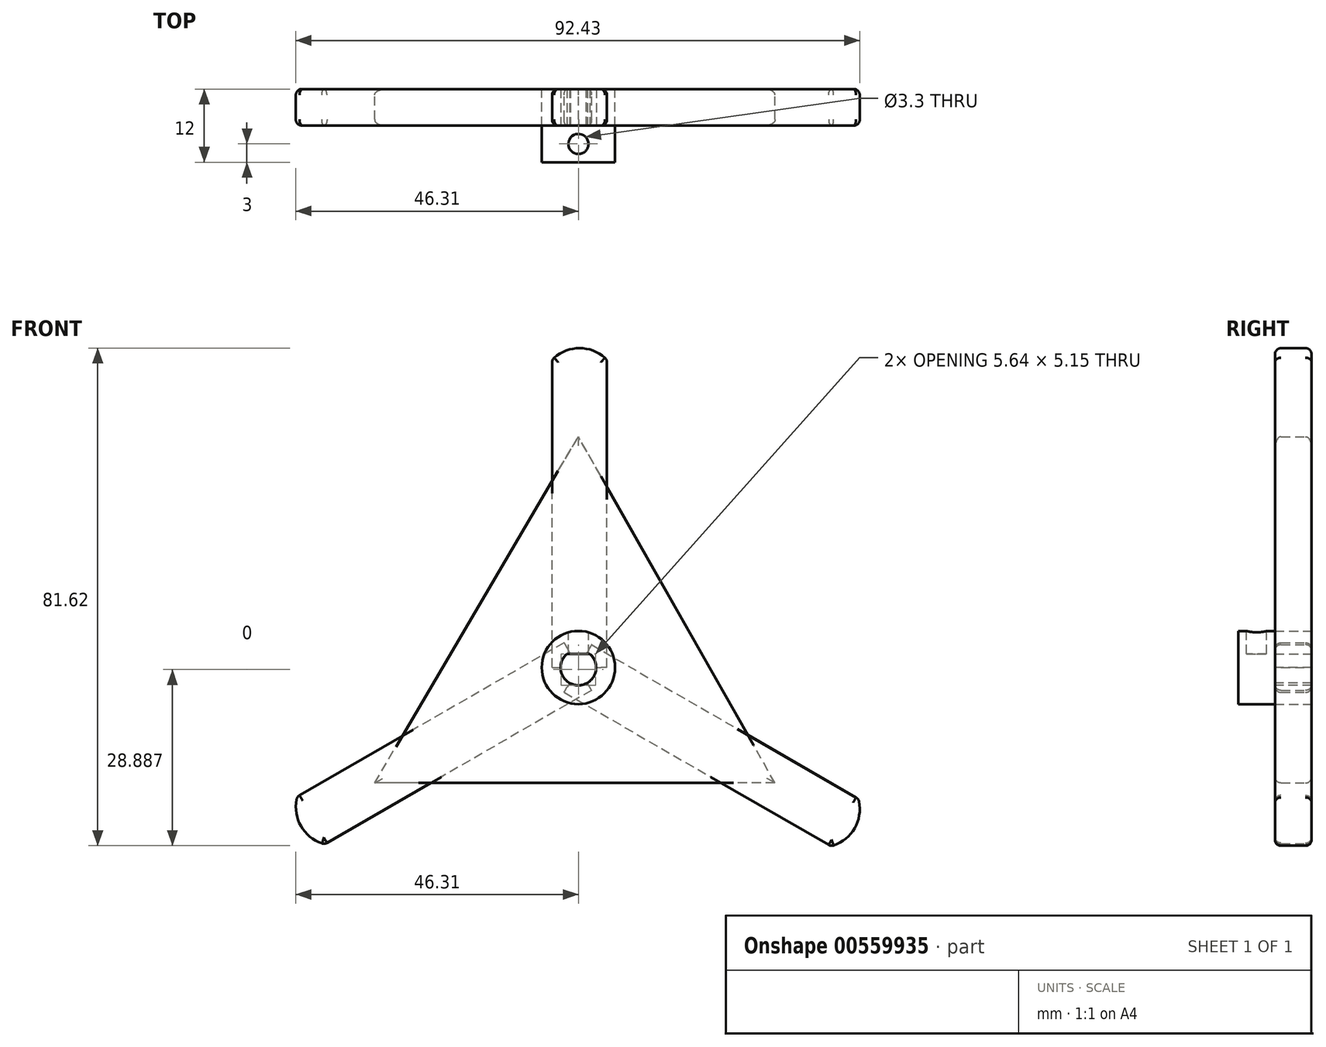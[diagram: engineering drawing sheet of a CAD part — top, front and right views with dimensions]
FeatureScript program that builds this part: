
annotation { "Feature Type Name" : "Feature", "Feature Type Description" : "" }
export const myFeature = defineFeature(function(context is Context, id is Id, definition is map)
    precondition{}
    {
        {
            assignVariable(context, id + "F0", {"name" : "thick", "anyValue" : 6});
        }
        {
            assignVariable(context, id + "F1", {"name" : "bushingWide", "anyValue" : 12});
        }
        {
            assignVariable(context, id + "F2", {"name" : "bushingDiam", "anyValue" : 12});
        }
        {
            assignVariable(context, id + "F3", {"name" : "filletRad", "anyValue" : 1});
        }
        {
            var Q0;
            Q0=qCreatedBy(makeId("Front.planeOp"),FACE);
            var sketch = newSketch(context, id + "F4", { "sketchPlane" : qUnion([Q0])});
            skLineSegment(sketch, "E0.bottom", {"start": v(-4.3, 0) * mm, "end": v(4.7, 0) * mm});
            skLineSegment(sketch, "E0.top", {"start": v(-4.3, 50.5) * mm, "end": v(4.7, 50.5) * mm});
            skLineSegment(sketch, "E0.left", {"start": v(-4.3, 0) * mm, "end": v(-4.3, 50.5) * mm});
            skLineSegment(sketch, "E0.right", {"start": v(4.7, 0) * mm, "end": v(4.7, 50.5) * mm});
            skArc(sketch, "E1", {"start": v(4.7, 50.5) * mm, "mid": v(0.2, 52.4) * mm, "end": v(-4.3, 50.5) * mm});
            skSolve(sketch);
        }
        {
            var Q0;
            Q0=qCreatedBy(makeId("Right.planeOp"),FACE);
            var sketch = newSketch(context, id + "F5", { "sketchPlane" : qUnion([Q0])});
            skLineSegment(sketch, "E2", {"start": v(0, 0) * mm, "end": v(-42.63, 0) * mm});
            skSolve(sketch);
        }
        {
            var Q0;
            Q0 = qSketchRegion(id + "F4", true);
            extrude(context, id + "F6", {"entities" : qUnion([Q0]), "depth" : (getVariable(context, 'thick')) * mm, "offsetDistance" : 25 * mm});
        }
        {
            var Q0;
            Q0=makeQuery(id+"F6.opExtrude","SWEPT_BODY",BODY,{"disambiguationData":[OSD([sQuery(id+"F4.wireOp",EDGE,"E0.bottom"),sQuery(id+"F4.wireOp",EDGE,"E0.left"),sQuery(id+"F4.wireOp",EDGE,"E0.right"),sQuery(id+"F4.wireOp",EDGE,"E1")])]});
            var Q1;
            Q1=sQuery(id+"F5.wireOp",EDGE,"E2");
            transform(context, id + "F7", {"entities" : qUnion([Q0]), "transformType" : TransformType.ROTATION, "transformAxis" : qUnion([Q1]), "angle" : 120 * degree, "makeCopy" : true});
        }
        {
            var Q0;
            Q0=makeQuery(id+"F6.opExtrude","SWEPT_BODY",BODY,{"disambiguationData":[OSD([sQuery(id+"F4.wireOp",EDGE,"E0.bottom"),sQuery(id+"F4.wireOp",EDGE,"E0.left"),sQuery(id+"F4.wireOp",EDGE,"E0.right"),sQuery(id+"F4.wireOp",EDGE,"E1")])]});
            var Q1;
            Q1=sQuery(id+"F5.wireOp",EDGE,"E2");
            transform(context, id + "F8", {"entities" : qUnion([Q0]), "transformType" : TransformType.ROTATION, "transformAxis" : qUnion([Q1]), "angle" : 240 * degree, "makeCopy" : true});
        }
        {
            var Q0;
            Q0=qCreatedBy(makeId("Front.planeOp"),FACE);
            var sketch = newSketch(context, id + "F9", { "sketchPlane" : qUnion([Q0])});
            skLineSegment(sketch, "E3", {"start": v(-1.88, 2.23) * mm, "end": v(1.88, 2.23) * mm});
            skCircle(sketch, "E4", {"center": v(0, 0) * mm, "radius": 6 * mm});
            skArc(sketch, "E5", {"start": v(-1.88, 2.23) * mm, "mid": v(0, -2.92) * mm, "end": v(1.88, 2.23) * mm});
            skSolve(sketch);
        }
        {
            var Q0;
            Q0=qCreatedBy(makeId("Front.planeOp"),FACE);
            var sketch = newSketch(context, id + "F10", { "sketchPlane" : qUnion([Q0])});
            skLineSegment(sketch, "E6", {"start": v(0, 0) * mm, "end": v(32.23, -18.94) * mm});
            skLineSegment(sketch, "E7", {"start": v(0, 0) * mm, "end": v(-33.39, -18.94) * mm});
            skLineSegment(sketch, "E8", {"start": v(0, 0) * mm, "end": v(0, 37.88) * mm});
            skLineSegment(sketch, "E9", {"start": v(-33.39, -18.94) * mm, "end": v(0, 37.88) * mm});
            skLineSegment(sketch, "E10", {"start": v(32.23, -18.94) * mm, "end": v(0, 37.88) * mm});
            skLineSegment(sketch, "E11", {"start": v(32.23, -18.94) * mm, "end": v(-33.39, -18.94) * mm});
            skSolve(sketch);
        }
        {
            var Q0;
            Q0=makeQuery(id+"F10.imprint","IMPRINT",FACE,{"disambiguationData":[TD([[makeQuery(id+"F10.imprint","IMPRINT",EDGE,{"derivedFrom":sQuery(id+"F10.wireOp",EDGE,"E7")}),-1.0]])]});
            var Q1;
            Q1=makeQuery(id+"F10.imprint","IMPRINT",FACE,{"disambiguationData":[TD([[makeQuery(id+"F10.imprint","IMPRINT",EDGE,{"derivedFrom":sQuery(id+"F10.wireOp",EDGE,"E6")}),1.0]])]});
            var Q2;
            Q2=makeQuery(id+"F10.imprint","IMPRINT",FACE,{"disambiguationData":[TD([[makeQuery(id+"F10.imprint","IMPRINT",EDGE,{"derivedFrom":sQuery(id+"F10.wireOp",EDGE,"E6")}),-1.0]])]});
            extrude(context, id + "F11", {"entities" : qUnion([Q0, Q1, Q2]), "depth" : (getVariable(context, 'thick')) * mm, "offsetDistance" : 25 * mm});
        }
        {
            var Q0;
            Q0 = qSketchRegion(id + "F9", true);
            extrude(context, id + "F12", {"entities" : qUnion([Q0]), "depth" : (getVariable(context, 'bushingWide')) * mm, "offsetDistance" : 25 * mm});
        }
        {
            var Q0;
            Q0=qCreatedBy(makeId("Top.planeOp"),FACE);
            cPlane(context, id + "F13", {"entities" : qUnion([Q0]), "cplaneType" : CPlaneType.OFFSET, "offset" : (getVariable(context, 'bushingDiam') / 2) * mm, "width" : 150 * mm, "height" : 150 * mm});
        }
        {
            var Q0;
            Q0=qCreatedBy(id+"F13.planeOp",FACE);
            var sketch = newSketch(context, id + "F14", { "sketchPlane" : qUnion([Q0])});
            skPoint(sketch, "E12", {"position": v(0, -9) * mm});
            skSolve(sketch);
        }
        {
            var Q0;
            Q0=sQuery(id+"F14.wireOp",VERTEX,"E12");
            var Q1;
            Q1=makeQuery(id+"F12.opExtrude","SWEPT_BODY",BODY,{"disambiguationData":[OSD([sQuery(id+"F9.wireOp",EDGE,"E3"),sQuery(id+"F9.wireOp",EDGE,"E4"),sQuery(id+"F9.wireOp",EDGE,"E5")])]});
            hole(context, id + "F15", {"style" : HoleStyle.SIMPLE, "endStyle" : HoleEndStyle.BLIND, "standardTappedOrClearance" : lookupTablePath({ "standard" : "ISO", "engagement" : "75%", "pitch" : "0.7 mm", "size" : "M4", "type" : "Tapped" }), "standardBlindInLast" : lookupTablePath({ "standard" : "ISO", "engagement" : "75%", "pitch" : "0.7 mm", "size" : "M4", "type" : "Tapped" }), "holeDiameter" : 3.3 * mm, "showTappedDepth" : true, "holeDepth" : 6 * mm, "isTappedThrough" : true, "tappedDepth" : (getVariable(context, 'bushingDiam') / 2) * mm, "tapClearance" : 0, "locations" : qUnion([Q0]), "scope" : qUnion([Q1]), "majorDiameter" : 4 * mm});
        }
        {
            var Q0;
            Q0=makeQuery(id+"F11.opExtrude","CAP_EDGE",EDGE,{"disambiguationData":[OSD([sQuery(id+"F10.wireOp",EDGE,"E9")])],"isStart":false});
            var Q1;
            Q1=makeQuery(id+"F6.opExtrude","CAP_EDGE",EDGE,{"disambiguationData":[OSD([sQuery(id+"F4.wireOp",EDGE,"E0.left")])],"isStart":false});
            var Q2;
            Q2=makeQuery(id+"F6.opExtrude","CAP_EDGE",EDGE,{"disambiguationData":[OSD([sQuery(id+"F4.wireOp",EDGE,"E1")])],"isStart":false});
            var Q3;
            Q3=makeQuery(id+"F6.opExtrude","CAP_EDGE",EDGE,{"disambiguationData":[OSD([sQuery(id+"F4.wireOp",EDGE,"E0.right")])],"isStart":false});
            var Q4;
            Q4=makeQuery(id+"F11.opExtrude","CAP_EDGE",EDGE,{"disambiguationData":[OSD([sQuery(id+"F10.wireOp",EDGE,"E10")])],"isStart":false});
            var Q5;
            Q5=makeQuery(id+"F8.opPattern","COPY",EDGE,{"derivedFrom":makeQuery(id+"F6.opExtrude","CAP_EDGE",EDGE,{"disambiguationData":[OSD([sQuery(id+"F4.wireOp",EDGE,"E0.left")])],"isStart":false}),"instanceName":"1"});
            var Q6;
            Q6=makeQuery(id+"F8.opPattern","COPY",EDGE,{"derivedFrom":makeQuery(id+"F6.opExtrude","CAP_EDGE",EDGE,{"disambiguationData":[OSD([sQuery(id+"F4.wireOp",EDGE,"E1")])],"isStart":false}),"instanceName":"1"});
            var Q7;
            Q7=makeQuery(id+"F11.opExtrude","CAP_EDGE",EDGE,{"disambiguationData":[OSD([sQuery(id+"F10.wireOp",EDGE,"E11")])],"isStart":false});
            var Q8;
            Q8=makeQuery(id+"F7.opPattern","COPY",EDGE,{"derivedFrom":makeQuery(id+"F6.opExtrude","CAP_EDGE",EDGE,{"disambiguationData":[OSD([sQuery(id+"F4.wireOp",EDGE,"E0.left")])],"isStart":false}),"instanceName":"1"});
            var Q9;
            Q9=makeQuery(id+"F8.opPattern","COPY",EDGE,{"derivedFrom":makeQuery(id+"F6.opExtrude","CAP_EDGE",EDGE,{"disambiguationData":[OSD([sQuery(id+"F4.wireOp",EDGE,"E0.right")])],"isStart":false}),"instanceName":"1"});
            var Q10;
            Q10=makeQuery(id+"F7.opPattern","COPY",EDGE,{"derivedFrom":makeQuery(id+"F6.opExtrude","CAP_EDGE",EDGE,{"disambiguationData":[OSD([sQuery(id+"F4.wireOp",EDGE,"E1")])],"isStart":false}),"instanceName":"1"});
            var Q11;
            Q11=makeQuery(id+"F7.opPattern","COPY",EDGE,{"derivedFrom":makeQuery(id+"F6.opExtrude","CAP_EDGE",EDGE,{"disambiguationData":[OSD([sQuery(id+"F4.wireOp",EDGE,"E0.right")])],"isStart":false}),"instanceName":"1"});
            fillet(context, id + "F16", {"entities" : qUnion([Q0, Q1, Q2, Q3, Q4, Q5, Q6, Q7, Q8, Q9, Q10, Q11]), "radius" : (getVariable(context, 'filletRad')) * mm, "tangentPropagation" : true, "allowEdgeOverflow" : false});
        }
        {
            var Q0;
            Q0=makeQuery(id+"F11.opExtrude","CAP_EDGE",EDGE,{"disambiguationData":[OSD([sQuery(id+"F10.wireOp",EDGE,"E11")])],"isStart":true});
            var Q1;
            Q1=makeQuery(id+"F7.opPattern","COPY",EDGE,{"derivedFrom":makeQuery(id+"F6.opExtrude","CAP_EDGE",EDGE,{"disambiguationData":[OSD([sQuery(id+"F4.wireOp",EDGE,"E0.left")])],"isStart":true}),"instanceName":"1"});
            var Q2;
            Q2=makeQuery(id+"F7.opPattern","COPY",EDGE,{"derivedFrom":makeQuery(id+"F6.opExtrude","CAP_EDGE",EDGE,{"disambiguationData":[OSD([sQuery(id+"F4.wireOp",EDGE,"E1")])],"isStart":true}),"instanceName":"1"});
            var Q3;
            Q3=makeQuery(id+"F7.opPattern","COPY",EDGE,{"derivedFrom":makeQuery(id+"F6.opExtrude","CAP_EDGE",EDGE,{"disambiguationData":[OSD([sQuery(id+"F4.wireOp",EDGE,"E0.right")])],"isStart":true}),"instanceName":"1"});
            var Q4;
            Q4=makeQuery(id+"F11.opExtrude","CAP_EDGE",EDGE,{"disambiguationData":[OSD([sQuery(id+"F10.wireOp",EDGE,"E9")])],"isStart":true});
            var Q5;
            Q5=makeQuery(id+"F6.opExtrude","CAP_EDGE",EDGE,{"disambiguationData":[OSD([sQuery(id+"F4.wireOp",EDGE,"E1")])],"isStart":true});
            var Q6;
            Q6=makeQuery(id+"F6.opExtrude","CAP_EDGE",EDGE,{"disambiguationData":[OSD([sQuery(id+"F4.wireOp",EDGE,"E0.left")])],"isStart":true});
            var Q7;
            Q7=makeQuery(id+"F11.opExtrude","CAP_EDGE",EDGE,{"disambiguationData":[OSD([sQuery(id+"F10.wireOp",EDGE,"E10")])],"isStart":true});
            var Q8;
            Q8=makeQuery(id+"F8.opPattern","COPY",EDGE,{"derivedFrom":makeQuery(id+"F6.opExtrude","CAP_EDGE",EDGE,{"disambiguationData":[OSD([sQuery(id+"F4.wireOp",EDGE,"E0.left")])],"isStart":true}),"instanceName":"1"});
            var Q9;
            Q9=makeQuery(id+"F8.opPattern","COPY",EDGE,{"derivedFrom":makeQuery(id+"F6.opExtrude","CAP_EDGE",EDGE,{"disambiguationData":[OSD([sQuery(id+"F4.wireOp",EDGE,"E0.right")])],"isStart":true}),"instanceName":"1"});
            var Q10;
            Q10=makeQuery(id+"F8.opPattern","COPY",EDGE,{"derivedFrom":makeQuery(id+"F6.opExtrude","CAP_EDGE",EDGE,{"disambiguationData":[OSD([sQuery(id+"F4.wireOp",EDGE,"E1")])],"isStart":true}),"instanceName":"1"});
            var Q11;
            Q11=makeQuery(id+"F6.opExtrude","CAP_EDGE",EDGE,{"disambiguationData":[OSD([sQuery(id+"F4.wireOp",EDGE,"E0.right")])],"isStart":true});
            fillet(context, id + "F17", {"entities" : qUnion([Q0, Q1, Q2, Q3, Q4, Q5, Q6, Q7, Q8, Q9, Q10, Q11]), "radius" : (getVariable(context, 'filletRad')) * mm, "tangentPropagation" : true, "allowEdgeOverflow" : false});
        }
        {
            var Q0;
            Q0=makeQuery(id+"F6.opExtrude","SWEPT_EDGE",EDGE,{"disambiguationData":[OSD([sQuery(id+"F4.wireOp",EDGE,"E0.top"),sQuery(id+"F4.wireOp",EDGE,"E0.right"),sQuery(id+"F4.wireOp",EDGE,"E1")])]});
            var Q1;
            Q1=makeQuery(id+"F8.opPattern","COPY",EDGE,{"derivedFrom":makeQuery(id+"F6.opExtrude","SWEPT_EDGE",EDGE,{"disambiguationData":[OSD([sQuery(id+"F4.wireOp",EDGE,"E0.top"),sQuery(id+"F4.wireOp",EDGE,"E0.left"),sQuery(id+"F4.wireOp",EDGE,"E1")])]}),"instanceName":"1"});
            var Q2;
            Q2=makeQuery(id+"F8.opPattern","COPY",EDGE,{"derivedFrom":makeQuery(id+"F6.opExtrude","SWEPT_EDGE",EDGE,{"disambiguationData":[OSD([sQuery(id+"F4.wireOp",EDGE,"E0.top"),sQuery(id+"F4.wireOp",EDGE,"E0.right"),sQuery(id+"F4.wireOp",EDGE,"E1")])]}),"instanceName":"1"});
            var Q3;
            Q3=makeQuery(id+"F7.opPattern","COPY",EDGE,{"derivedFrom":makeQuery(id+"F6.opExtrude","SWEPT_EDGE",EDGE,{"disambiguationData":[OSD([sQuery(id+"F4.wireOp",EDGE,"E0.top"),sQuery(id+"F4.wireOp",EDGE,"E0.left"),sQuery(id+"F4.wireOp",EDGE,"E1")])]}),"instanceName":"1"});
            var Q4;
            Q4=makeQuery(id+"F7.opPattern","COPY",EDGE,{"derivedFrom":makeQuery(id+"F6.opExtrude","SWEPT_EDGE",EDGE,{"disambiguationData":[OSD([sQuery(id+"F4.wireOp",EDGE,"E0.top"),sQuery(id+"F4.wireOp",EDGE,"E0.right"),sQuery(id+"F4.wireOp",EDGE,"E1")])]}),"instanceName":"1"});
            var Q5;
            Q5=makeQuery(id+"F6.opExtrude","SWEPT_EDGE",EDGE,{"disambiguationData":[OSD([sQuery(id+"F4.wireOp",EDGE,"E0.top"),sQuery(id+"F4.wireOp",EDGE,"E0.left"),sQuery(id+"F4.wireOp",EDGE,"E1")])]});
            fillet(context, id + "F18", {"entities" : qUnion([Q0, Q1, Q2, Q3, Q4, Q5]), "radius" : (getVariable(context, 'filletRad')) * mm, "tangentPropagation" : true, "allowEdgeOverflow" : false});
        }
        {
            var Q0;
            Q0=makeQuery(id+"F9.imprint","IMPRINT",FACE,{"disambiguationData":[TD([[makeQuery(id+"F9.imprint","IMPRINT",EDGE,{"derivedFrom":sQuery(id+"F9.wireOp",EDGE,"E3")}),-1.0]])]});
            extrude(context, id + "F19", {"entities" : qUnion([Q0]), "operationType" : NewBodyOperationType.REMOVE, "oppositeDirection" : true, "depth" : 25 * mm, "offsetDistance" : 25 * mm, "symmetric" : true});
        }
    });
